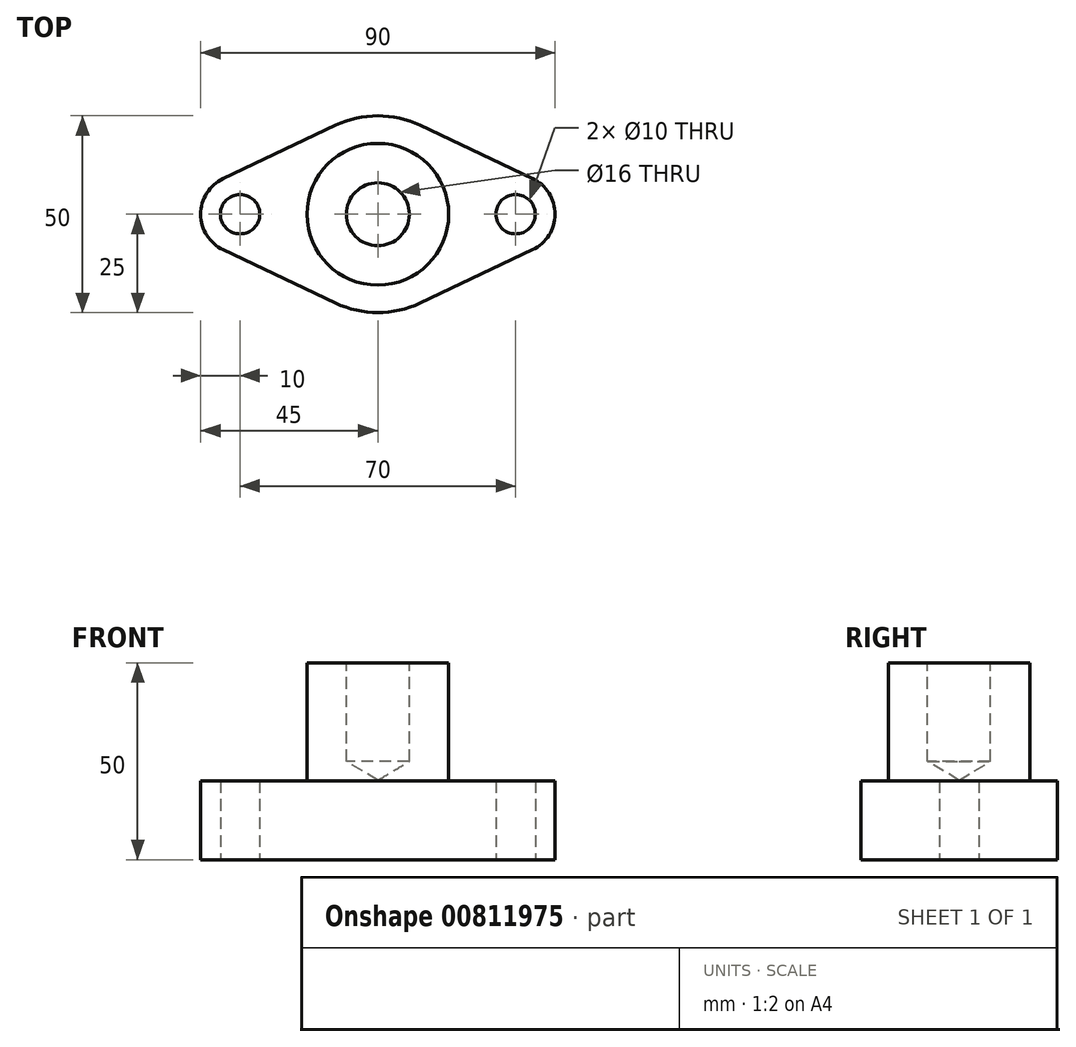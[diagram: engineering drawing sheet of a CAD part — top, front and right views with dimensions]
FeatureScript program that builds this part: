
annotation { "Feature Type Name" : "Feature", "Feature Type Description" : "" }
export const myFeature = defineFeature(function(context is Context, id is Id, definition is map)
    precondition{}
    {
        {
            var Q0;
            Q0=qCreatedBy(makeId("Top.planeOp"),FACE);
            var sketch = newSketch(context, id + "F0", { "sketchPlane" : qUnion([Q0])});
            skLineSegment(sketch, "E0", {"start": v(0, 0) * mm, "end": v(35, 0) * mm});
            skLineSegment(sketch, "E1", {"start": v(35, 0) * mm, "end": v(-35, 0) * mm});
            skCircle(sketch, "E2", {"center": v(-35, 0) * mm, "radius": 10 * mm});
            skCircle(sketch, "E3", {"center": v(35, 0) * mm, "radius": 10 * mm});
            skCircle(sketch, "E4", {"center": v(0, 0) * mm, "radius": 25 * mm});
            skLineSegment(sketch, "E5", {"start": v(-58.33, 0) * mm, "end": v(0, 27.67) * mm});
            skLineSegment(sketch, "E6", {"start": v(58.33, 0) * mm, "end": v(0, 27.67) * mm});
            skLineSegment(sketch, "E7", {"start": v(-58.33, 0) * mm, "end": v(0, -27.67) * mm});
            skLineSegment(sketch, "E8", {"start": v(58.33, 0) * mm, "end": v(0, -27.67) * mm});
            skSolve(sketch);
        }
        {
            var Q0;
            Q0 = qSketchRegion(id + "F0", true);
            extrude(context, id + "F1", {"entities" : qUnion([Q0]), "depth" : 20 * mm, "offsetDistance" : 25 * mm});
        }
        {
            var Q0;
            Q0=makeQuery(id+"F1.opExtrude","CAP_FACE",FACE,{"disambiguationData":[OSD([sQuery(id+"F0.wireOp",EDGE,"E5"),sQuery(id+"F0.wireOp",EDGE,"E6"),sQuery(id+"F0.wireOp",EDGE,"E7"),sQuery(id+"F0.wireOp",EDGE,"E8")])],"isStart":false});
            var sketch = newSketch(context, id + "F2", { "sketchPlane" : qUnion([Q0])});
            skCircle(sketch, "E9", {"center": v(0, 0) * mm, "radius": 18 * mm});
            skSolve(sketch);
        }
        {
            var Q0;
            Q0=makeQuery(id+"F2.imprint","IMPRINT",FACE,{"disambiguationData":[TD([[makeQuery(id+"F2.imprint","IMPRINT",EDGE,{"derivedFrom":sQuery(id+"F2.wireOp",EDGE,"E9")}),1.0]])]});
            extrude(context, id + "F3", {"entities" : qUnion([Q0]), "operationType" : NewBodyOperationType.ADD, "depth" : 30 * mm, "offsetDistance" : 25 * mm});
        }
        {
            var Q0;
            Q0=qCreatedBy(makeId("Top.planeOp"),FACE);
            var sketch = newSketch(context, id + "F4", { "sketchPlane" : qUnion([Q0])});
            skLineSegment(sketch, "E10", {"start": v(0, 0) * mm, "end": v(35, 0) * mm});
            skLineSegment(sketch, "E11", {"start": v(35, 0) * mm, "end": v(-35, 0) * mm});
            skPoint(sketch, "E11.endSnap0", {"position": v(17.5, 0) * mm});
            skPoint(sketch, "E12", {"position": v(-35, 0) * mm});
            skPoint(sketch, "E13", {"position": v(0, 0) * mm});
            skPoint(sketch, "E14", {"position": v(35, 0) * mm});
            skSolve(sketch);
        }
        {
            var Q0;
            Q0=sQuery(id+"F0.wireOp",VERTEX,"E1.end");
            var Q1;
            Q1=sQuery(id+"F4.wireOp",VERTEX,"E14");
            var Q2;
            Q2=makeQuery(id+"F1.opExtrude","SWEPT_BODY",BODY,{"disambiguationData":[OSD([sQuery(id+"F0.wireOp",EDGE,"E5"),sQuery(id+"F0.wireOp",EDGE,"E6"),sQuery(id+"F0.wireOp",EDGE,"E7"),sQuery(id+"F0.wireOp",EDGE,"E8")])]});
            hole(context, id + "F5", {"style" : HoleStyle.SIMPLE, "endStyle" : HoleEndStyle.BLIND, "oppositeDirection" : true, "holeDiameter" : 10 * mm, "majorDiameter" : 5 * mm, "holeDepth" : 20 * mm, "isTappedThrough" : true, "tappedDepth" : 12 * mm, "tapClearance" : 3, "locations" : qUnion([Q0, Q1]), "scope" : qUnion([Q2])});
        }
        {
            var Q0;
            Q0=makeQuery(id+"F3.opExtrude","CAP_FACE",FACE,{"disambiguationData":[OSD([sQuery(id+"F2.wireOp",EDGE,"E9")])],"isStart":false});
            var sketch = newSketch(context, id + "F6", { "sketchPlane" : qUnion([Q0])});
            skPoint(sketch, "E15", {"position": v(0, 0) * mm});
            skSolve(sketch);
        }
        {
            var Q0;
            Q0=sQuery(id+"F6.wireOp",VERTEX,"E15");
            var Q1;
            Q1=makeQuery(id+"F1.opExtrude","SWEPT_BODY",BODY,{"disambiguationData":[OSD([sQuery(id+"F0.wireOp",EDGE,"E5"),sQuery(id+"F0.wireOp",EDGE,"E6"),sQuery(id+"F0.wireOp",EDGE,"E7"),sQuery(id+"F0.wireOp",EDGE,"E8")])]});
            hole(context, id + "F7", {"style" : HoleStyle.SIMPLE, "endStyle" : HoleEndStyle.BLIND, "holeDiameter" : 16 * mm, "majorDiameter" : 5 * mm, "holeDepth" : 25 * mm, "isTappedThrough" : true, "tappedDepth" : 12 * mm, "tapClearance" : 3, "locations" : qUnion([Q0]), "scope" : qUnion([Q1])});
        }
        {
            var Q0;
            Q0=makeQuery(id+"F1.opExtrude","SWEPT_EDGE",EDGE,{"disambiguationData":[OSD([sQuery(id+"F0.wireOp",EDGE,"E7"),sQuery(id+"F0.wireOp",EDGE,"E8")])]});
            var Q1;
            Q1=makeQuery(id+"F1.opExtrude","SWEPT_EDGE",EDGE,{"disambiguationData":[OSD([sQuery(id+"F0.wireOp",EDGE,"E5"),sQuery(id+"F0.wireOp",EDGE,"E6")])]});
            fillet(context, id + "F8", {"entities" : qUnion([Q0, Q1]), "radius" : 25 * mm, "tangentPropagation" : true, "allowEdgeOverflow" : false});
        }
        {
            var Q0;
            Q0=makeQuery(id+"F1.opExtrude","SWEPT_EDGE",EDGE,{"disambiguationData":[OSD([sQuery(id+"F0.wireOp",EDGE,"E5"),sQuery(id+"F0.wireOp",EDGE,"E7")])]});
            var Q1;
            Q1=makeQuery(id+"F1.opExtrude","SWEPT_EDGE",EDGE,{"disambiguationData":[OSD([sQuery(id+"F0.wireOp",EDGE,"E6"),sQuery(id+"F0.wireOp",EDGE,"E8")])]});
            fillet(context, id + "F9", {"entities" : qUnion([Q0, Q1]), "radius" : 10 * mm, "tangentPropagation" : true, "allowEdgeOverflow" : false});
        }
    });
